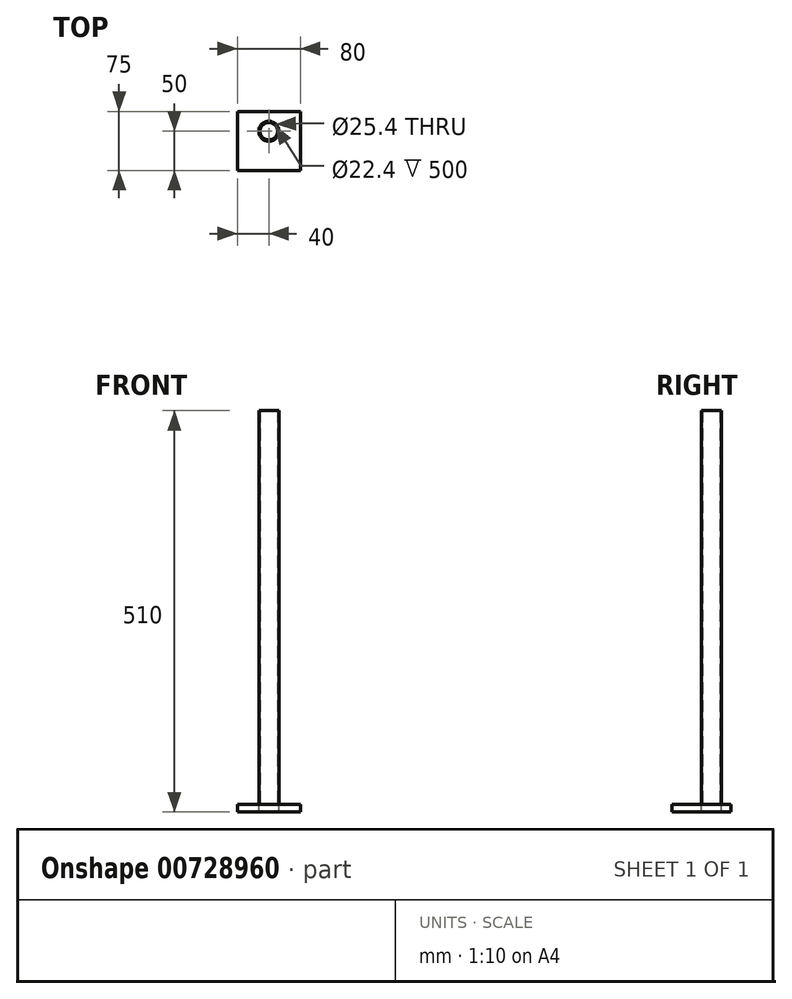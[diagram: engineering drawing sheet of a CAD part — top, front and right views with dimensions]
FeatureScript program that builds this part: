
annotation { "Feature Type Name" : "Feature", "Feature Type Description" : "" }
export const myFeature = defineFeature(function(context is Context, id is Id, definition is map)
    precondition{}
    {
        {
            var Q0;
            Q0=qCreatedBy(makeId("Top.planeOp"),FACE);
            var sketch = newSketch(context, id + "F0", { "sketchPlane" : qUnion([Q0])});
            skCircle(sketch, "E0", {"center": v(0, 0) * mm, "radius": 12.7 * mm});
            skCircle(sketch, "E1", {"center": v(0, 0) * mm, "radius": 11.2 * mm});
            skSolve(sketch);
        }
        {
            var Q0;
            Q0 = qSketchRegion(id + "F0", true);
            extrude(context, id + "F1", {"entities" : qUnion([Q0]), "depth" : 500 * mm, "offsetDistance" : 25 * mm});
        }
        {
            var Q0;
            Q0=qCreatedBy(makeId("Top.planeOp"),FACE);
            var sketch = newSketch(context, id + "F2", { "sketchPlane" : qUnion([Q0])});
            skLineSegment(sketch, "E2.bottom", {"start": v(-40, 25) * mm, "end": v(40, 25) * mm});
            skLineSegment(sketch, "E2.top", {"start": v(-40, -50) * mm, "end": v(40, -50) * mm});
            skLineSegment(sketch, "E2.left", {"start": v(-40, 25) * mm, "end": v(-40, -50) * mm});
            skLineSegment(sketch, "E2.right", {"start": v(40, 25) * mm, "end": v(40, -50) * mm});
            skPoint(sketch, "E3", {"position": v(0, 25) * mm});
            skCircle(sketch, "E4", {"center": v(0, 0) * mm, "radius": 12.7 * mm});
            skSolve(sketch);
        }
        {
            var Q0;
            Q0 = qSketchRegion(id + "F2", true);
            extrude(context, id + "F3", {"entities" : qUnion([Q0]), "oppositeDirection" : true, "depth" : 10 * mm, "offsetDistance" : 25 * mm});
        }
    });
